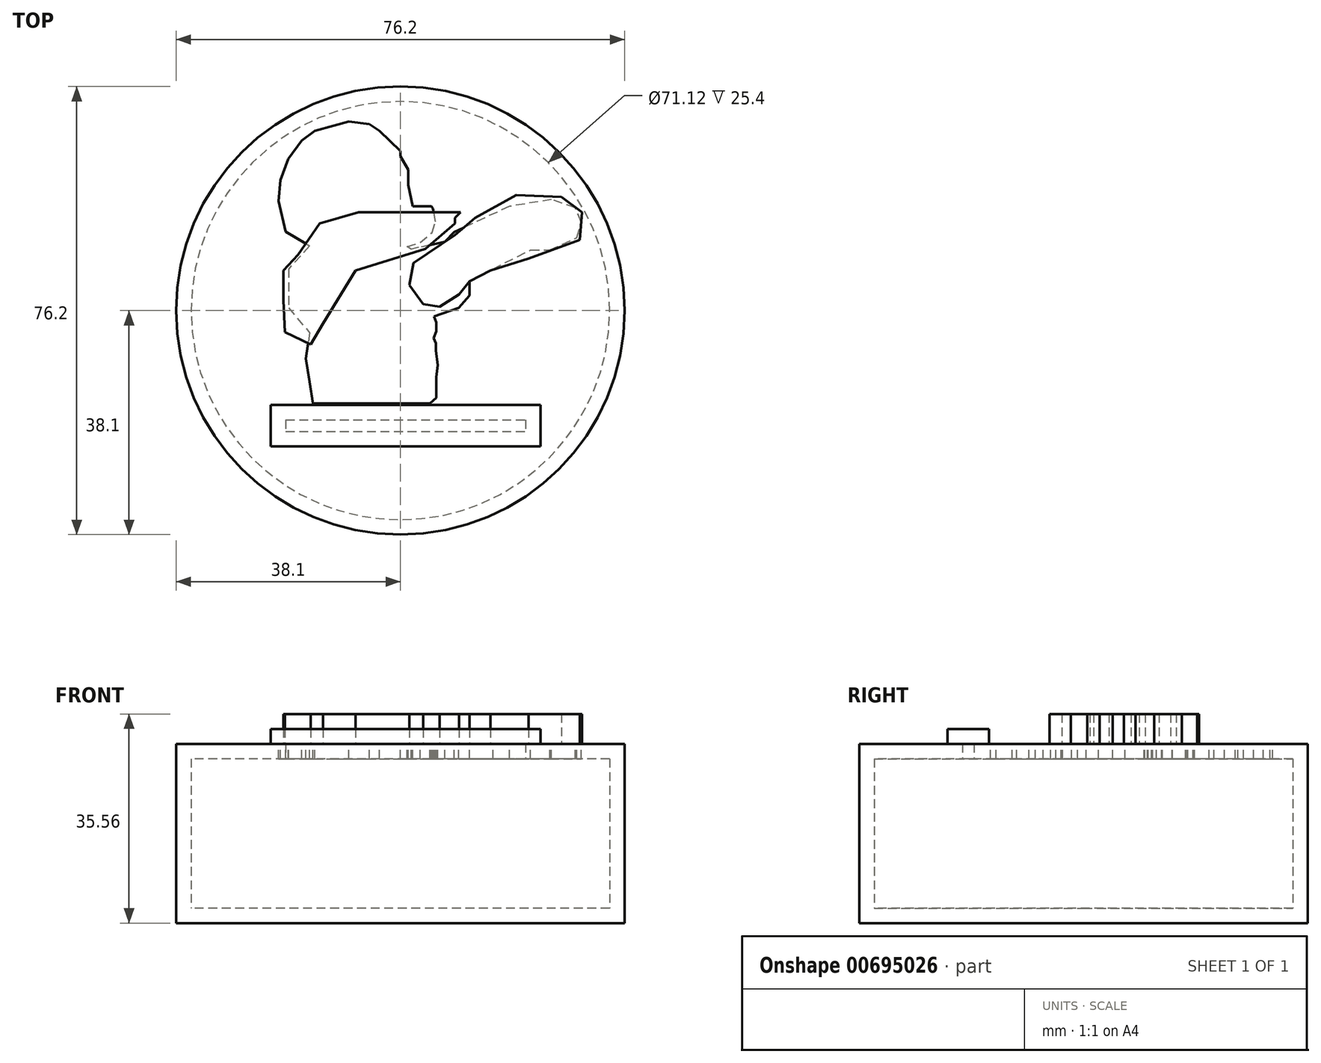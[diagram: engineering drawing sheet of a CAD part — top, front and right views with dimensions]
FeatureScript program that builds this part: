
annotation { "Feature Type Name" : "Feature", "Feature Type Description" : "" }
export const myFeature = defineFeature(function(context is Context, id is Id, definition is map)
    precondition{}
    {
        {
            var Q0;
            Q0=qCreatedBy(makeId("Top.planeOp"),FACE);
            var sketch = newSketch(context, id + "F0", { "sketchPlane" : qUnion([Q0])});
            skCircle(sketch, "E0", {"center": v(0, 0) * mm, "radius": 38.1 * mm});
            skSolve(sketch);
        }
        {
            var Q0;
            Q0 = qSketchRegion(id + "F0", true);
            extrude(context, id + "F1", {"entities" : qUnion([Q0]), "depth" : 30.48 * mm, "offsetDistance" : 25.4 * mm});
        }
        {
            var Q0;
            Q0=makeQuery(id+"F1.opExtrude","CAP_FACE",FACE,{"disambiguationData":[OSD([sQuery(id+"F0.wireOp",EDGE,"E0")])],"isStart":false});
            var sketch = newSketch(context, id + "F2", { "sketchPlane" : qUnion([Q0])});
            skLineSegment(sketch, "E1.bottom", {"start": v(-22.02, -16.06) * mm, "end": v(23.8, -16.06) * mm});
            skLineSegment(sketch, "E1.top", {"start": v(-22.02, -23.07) * mm, "end": v(23.8, -23.07) * mm});
            skLineSegment(sketch, "E1.left", {"start": v(-22.02, -16.06) * mm, "end": v(-22.02, -23.07) * mm});
            skLineSegment(sketch, "E1.right", {"start": v(23.8, -16.06) * mm, "end": v(23.8, -23.07) * mm});
            skSolve(sketch);
        }
        {
            var Q0;
            Q0=makeQuery(id+"F2.imprint","IMPRINT",FACE,{"disambiguationData":[TD([[makeQuery(id+"F2.imprint","IMPRINT",EDGE,{"derivedFrom":sQuery(id+"F2.wireOp",EDGE,"E1.bottom")}),-1.0]])]});
            extrude(context, id + "F3", {"entities" : qUnion([Q0]), "operationType" : NewBodyOperationType.ADD, "depth" : 2.54 * mm, "offsetDistance" : 25.4 * mm});
        }
        {
            var Q0;
            Q0=makeQuery(id+"F1.opExtrude","CAP_FACE",FACE,{"disambiguationData":[OSD([sQuery(id+"F0.wireOp",EDGE,"E0")])],"isStart":false});
            var Q1;
            Q1=makeQuery(id+"F1.opExtrude","SWEPT_BODY",BODY,{"disambiguationData":[OSD([sQuery(id+"F0.wireOp",EDGE,"E0")])]});
            shell(context, id + "F4", {"isHollow" : true, "entities" : qUnion([Q0]), "parts" : qUnion([Q1]), "thickness" : 2.54 * mm});
        }
        {
            var Q0;
            Q0=makeQuery(id+"F1.opExtrude","CAP_FACE",FACE,{"disambiguationData":[OSD([sQuery(id+"F0.wireOp",EDGE,"E0")])],"isStart":false});
            var sketch = newSketch(context, id + "F5", { "sketchPlane" : qUnion([Q0])});
            skCircle(sketch, "E2", {"center": v(-18.26, -19.25) * mm, "radius": 2 * mm});
            skCircle(sketch, "E3", {"center": v(19.64, -19.43) * mm, "radius": 2.12 * mm});
            skSolve(sketch);
        }
        {
            var Q0;
            Q0=makeQuery(id+"F5.imprint","IMPRINT",FACE,{"disambiguationData":[TD([[makeQuery(id+"F5.imprint","IMPRINT",EDGE,{"derivedFrom":makeQuery(id+"F1.opExtrude","CAP_EDGE",EDGE,{"disambiguationData":[OSD([sQuery(id+"F0.wireOp",EDGE,"E0")])],"isStart":false})}),1.0]])]});
            var sketch = newSketch(context, id + "F6", { "sketchPlane" : qUnion([Q0])});
            skSolve(sketch);
        }
        {
            var Q0;
            Q0=makeQuery(id+"F6.imprint","IMPRINT",FACE,{"disambiguationData":[TD([[makeQuery(id+"F6.imprint","IMPRINT",EDGE,{"derivedFrom":makeQuery(id+"F5.imprint","IMPRINT",EDGE,{"derivedFrom":makeQuery(id+"F1.opExtrude","CAP_EDGE",EDGE,{"disambiguationData":[OSD([sQuery(id+"F0.wireOp",EDGE,"E0")])],"isStart":false})})}),1.0]])]});
            var sketch = newSketch(context, id + "F7", { "sketchPlane" : qUnion([Q0])});
            skLineSegment(sketch, "E4", {"start": v(-14.84, -15.77) * mm, "end": v(5, -15.77) * mm});
            skLineSegment(sketch, "E5", {"start": v(5, -15.77) * mm, "end": v(6.12, -14.84) * mm});
            skLineSegment(sketch, "E6", {"start": v(6.12, -14.84) * mm, "end": v(6.12, -11.34) * mm});
            skLineSegment(sketch, "E7", {"start": v(6.12, -11.34) * mm, "end": v(6.32, -9.27) * mm});
            skLineSegment(sketch, "E8", {"start": v(6.32, -9.27) * mm, "end": v(6.02, -6.81) * mm});
            skLineSegment(sketch, "E9", {"start": v(6.02, -6.81) * mm, "end": v(6, -5.57) * mm});
            skLineSegment(sketch, "E10", {"start": v(6, -5.57) * mm, "end": v(5.63, -4.68) * mm});
            skLineSegment(sketch, "E11", {"start": v(5.63, -4.68) * mm, "end": v(6.08, -3.56) * mm});
            skLineSegment(sketch, "E12", {"start": v(6.08, -3.56) * mm, "end": v(6.08, -2.02) * mm});
            skLineSegment(sketch, "E13", {"start": v(6.08, -2.02) * mm, "end": v(5.73, -1.03) * mm});
            skLineSegment(sketch, "E14", {"start": v(5.73, -1.03) * mm, "end": v(9.9, 0.44) * mm});
            skLineSegment(sketch, "E15", {"start": v(9.9, 0.44) * mm, "end": v(11.72, 2.55) * mm});
            skLineSegment(sketch, "E16", {"start": v(11.72, 2.55) * mm, "end": v(11.72, 4.97) * mm});
            skLineSegment(sketch, "E17", {"start": v(11.72, 4.97) * mm, "end": v(15.74, 7.09) * mm});
            skLineSegment(sketch, "E18", {"start": v(15.74, 7.09) * mm, "end": v(22.1, 10.3) * mm});
            skLineSegment(sketch, "E19", {"start": v(22.1, 10.3) * mm, "end": v(25.42, 10.3) * mm});
            skLineSegment(sketch, "E20", {"start": v(25.42, 10.3) * mm, "end": v(30, 12.42) * mm});
            skLineSegment(sketch, "E21", {"start": v(30, 12.42) * mm, "end": v(30.74, 15.05) * mm});
            skLineSegment(sketch, "E22", {"start": v(30.74, 15.05) * mm, "end": v(29.69, 17.48) * mm});
            skLineSegment(sketch, "E23", {"start": v(29.69, 17.48) * mm, "end": v(25.65, 18.9) * mm});
            skLineSegment(sketch, "E24", {"start": v(25.65, 18.9) * mm, "end": v(18.52, 17.7) * mm});
            skLineSegment(sketch, "E25", {"start": v(18.52, 17.7) * mm, "end": v(16.65, 16.84) * mm});
            skLineSegment(sketch, "E26", {"start": v(16.65, 16.84) * mm, "end": v(9.11, 13.36) * mm});
            skLineSegment(sketch, "E27", {"start": v(9.11, 13.36) * mm, "end": v(7.57, 11.73) * mm});
            skLineSegment(sketch, "E28", {"start": v(7.57, 11.73) * mm, "end": v(1.84, 10.45) * mm});
            skLineSegment(sketch, "E29", {"start": v(1.84, 10.45) * mm, "end": v(1.15, 10.85) * mm});
            skLineSegment(sketch, "E30", {"start": v(1.15, 10.85) * mm, "end": v(3.37, 11.57) * mm});
            skLineSegment(sketch, "E31", {"start": v(3.37, 11.57) * mm, "end": v(5.38, 13.3) * mm});
            skLineSegment(sketch, "E32", {"start": v(5.38, 13.3) * mm, "end": v(5.97, 15.1) * mm});
            skLineSegment(sketch, "E33", {"start": v(5.97, 15.1) * mm, "end": v(5.54, 17.36) * mm});
            skLineSegment(sketch, "E34", {"start": v(5.54, 17.36) * mm, "end": v(5.24, 17.72) * mm});
            skLineSegment(sketch, "E35", {"start": v(5.24, 17.72) * mm, "end": v(2.12, 17.72) * mm});
            skLineSegment(sketch, "E36", {"start": v(-3.54, 30.53) * mm, "end": v(-5.27, 31.71) * mm});
            skLineSegment(sketch, "E37", {"start": v(-16.78, 28.88) * mm, "end": v(-19.06, 25.79) * mm});
            skLineSegment(sketch, "E38", {"start": v(-19.06, 25.79) * mm, "end": v(-20.36, 22.2) * mm});
            skLineSegment(sketch, "E39", {"start": v(-20.36, 22.2) * mm, "end": v(-20.73, 18.65) * mm});
            skLineSegment(sketch, "E40", {"start": v(-20.73, 18.65) * mm, "end": v(-19.48, 13.4) * mm});
            skLineSegment(sketch, "E41", {"start": v(-19.48, 13.4) * mm, "end": v(-15.41, 10.98) * mm});
            skLineSegment(sketch, "E42", {"start": v(-15.41, 10.98) * mm, "end": v(-19.02, 7.09) * mm});
            skLineSegment(sketch, "E43", {"start": v(-19.02, 7.09) * mm, "end": v(-19.02, 0.44) * mm});
            skLineSegment(sketch, "E44", {"start": v(-19.02, 0.44) * mm, "end": v(-15.41, -3.77) * mm});
            skLineSegment(sketch, "E45", {"start": v(-15.41, -3.77) * mm, "end": v(-16.07, -8.2) * mm});
            skLineSegment(sketch, "E46", {"start": v(-16.07, -8.2) * mm, "end": v(-15.41, -12.12) * mm});
            skLineSegment(sketch, "E47", {"start": v(-15.41, -12.12) * mm, "end": v(-14.84, -15.77) * mm});
            skLineSegment(sketch, "E48", {"start": v(-16.78, 28.88) * mm, "end": v(-14.56, 30.54) * mm});
            skLineSegment(sketch, "E49", {"start": v(-14.56, 30.54) * mm, "end": v(-11.31, 31.44) * mm});
            skLineSegment(sketch, "E50", {"start": v(-11.31, 31.44) * mm, "end": v(-8.75, 32.13) * mm});
            skLineSegment(sketch, "E51", {"start": v(-8.75, 32.13) * mm, "end": v(-5.27, 31.71) * mm});
            skLineSegment(sketch, "E52", {"start": v(-3.54, 30.53) * mm, "end": v(0, 27.16) * mm});
            skLineSegment(sketch, "E53", {"start": v(0, 27.16) * mm, "end": v(0, 27.16) * mm});
            skLineSegment(sketch, "E54", {"start": v(0, 26.23) * mm, "end": v(1.34, 23.98) * mm});
            skLineSegment(sketch, "E55", {"start": v(1.34, 23.98) * mm, "end": v(1.34, 21.34) * mm});
            skLineSegment(sketch, "E56", {"start": v(1.34, 21.34) * mm, "end": v(2.12, 17.72) * mm});
            skLineSegment(sketch, "E57", {"start": v(0, 26.23) * mm, "end": v(0, 27.16) * mm});
            skSolve(sketch);
        }
        {
            var Q0;
            Q0 = qSketchRegion(id + "F7", true);
            extrude(context, id + "F8", {"entities" : qUnion([Q0]), "operationType" : NewBodyOperationType.REMOVE, "oppositeDirection" : true, "depth" : 9.9 * mm, "offsetDistance" : 25.4 * mm});
        }
        {
            var Q0;
            Q0=makeQuery(id+"F6.imprint","IMPRINT",FACE,{"disambiguationData":[TD([[makeQuery(id+"F6.imprint","IMPRINT",EDGE,{"derivedFrom":makeQuery(id+"F5.imprint","IMPRINT",EDGE,{"derivedFrom":makeQuery(id+"F1.opExtrude","CAP_EDGE",EDGE,{"disambiguationData":[OSD([sQuery(id+"F0.wireOp",EDGE,"E0")])],"isStart":false})})}),1.0]])]});
            var sketch = newSketch(context, id + "F9", { "sketchPlane" : qUnion([Q0])});
            skLineSegment(sketch, "E58", {"start": v(10.23, 16.72) * mm, "end": v(-7.13, 16.72) * mm});
            skLineSegment(sketch, "E59", {"start": v(-7.13, 16.72) * mm, "end": v(-13.7, 14.84) * mm});
            skLineSegment(sketch, "E60", {"start": v(-13.7, 14.84) * mm, "end": v(-17.4, 9.49) * mm});
            skLineSegment(sketch, "E61", {"start": v(-17.4, 9.49) * mm, "end": v(-19.9, 6.84) * mm});
            skLineSegment(sketch, "E62", {"start": v(-19.9, 6.84) * mm, "end": v(-19.9, 1.72) * mm});
            skLineSegment(sketch, "E63", {"start": v(-19.9, 1.72) * mm, "end": v(-19.66, -3.68) * mm});
            skLineSegment(sketch, "E64", {"start": v(-19.66, -3.68) * mm, "end": v(-15.27, -5.74) * mm});
            skLineSegment(sketch, "E65", {"start": v(-15.27, -5.74) * mm, "end": v(-13.15, -2.17) * mm});
            skLineSegment(sketch, "E66", {"start": v(-13.15, -2.17) * mm, "end": v(-7.6, 6.84) * mm});
            skLineSegment(sketch, "E67", {"start": v(4.24, 10.47) * mm, "end": v(-7.6, 6.84) * mm});
            skLineSegment(sketch, "E68", {"start": v(9.27, 14.8) * mm, "end": v(4.24, 10.47) * mm});
            skLineSegment(sketch, "E69", {"start": v(9.27, 14.8) * mm, "end": v(9.27, 15.75) * mm});
            skLineSegment(sketch, "E70", {"start": v(10.23, 16.72) * mm, "end": v(9.27, 15.75) * mm});
            skLineSegment(sketch, "E71", {"start": v(6.64, 0.68) * mm, "end": v(9.96, 2.75) * mm});
            skLineSegment(sketch, "E72", {"start": v(9.96, 2.75) * mm, "end": v(11.76, 4.96) * mm});
            skLineSegment(sketch, "E73", {"start": v(11.76, 4.96) * mm, "end": v(15.3, 6.84) * mm});
            skLineSegment(sketch, "E74", {"start": v(21.8, 8.83) * mm, "end": v(15.3, 6.84) * mm});
            skLineSegment(sketch, "E75", {"start": v(21.8, 8.83) * mm, "end": v(30.5, 12.02) * mm});
            skLineSegment(sketch, "E76", {"start": v(30.5, 12.02) * mm, "end": v(30.85, 16.72) * mm});
            skLineSegment(sketch, "E77", {"start": v(30.85, 16.72) * mm, "end": v(27.39, 19.35) * mm});
            skLineSegment(sketch, "E78", {"start": v(27.39, 19.35) * mm, "end": v(19.66, 19.61) * mm});
            skLineSegment(sketch, "E79", {"start": v(19.66, 19.61) * mm, "end": v(12.7, 15.75) * mm});
            skLineSegment(sketch, "E80", {"start": v(12.7, 15.75) * mm, "end": v(10.9, 14.23) * mm});
            skLineSegment(sketch, "E81", {"start": v(10.9, 14.23) * mm, "end": v(9.27, 12.86) * mm});
            skLineSegment(sketch, "E82", {"start": v(9.27, 12.86) * mm, "end": v(2.25, 8.08) * mm});
            skLineSegment(sketch, "E83", {"start": v(2.25, 8.08) * mm, "end": v(1.5, 4.34) * mm});
            skLineSegment(sketch, "E84", {"start": v(1.5, 4.34) * mm, "end": v(3.88, 1.08) * mm});
            skLineSegment(sketch, "E85", {"start": v(3.88, 1.08) * mm, "end": v(6.64, 0.68) * mm});
            skPoint(sketch, "E86", {"position": v(5.76, 10.47) * mm});
            skSolve(sketch);
        }
        {
            var Q0;
            Q0 = qSketchRegion(id + "F9", true);
            extrude(context, id + "F10", {"entities" : qUnion([Q0]), "operationType" : NewBodyOperationType.ADD, "depth" : 5.08 * mm, "offsetDistance" : 25.4 * mm});
        }
    });
